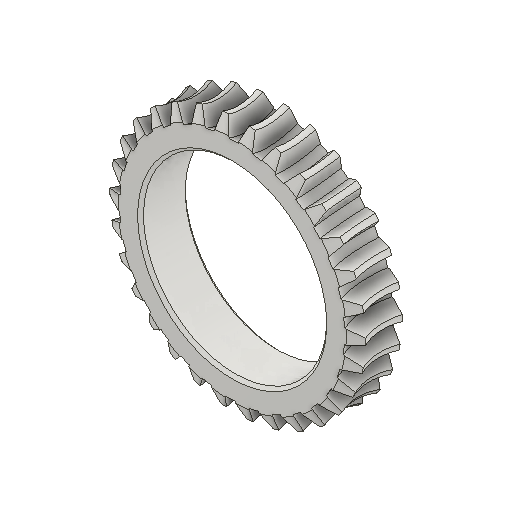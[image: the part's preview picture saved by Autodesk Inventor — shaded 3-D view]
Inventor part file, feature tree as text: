
AUTODESK INVENTOR PART (.ipt)
format: ipt  version: 2024.1 (Build 281209000, 209)  size: 570,368 bytes
history: native  units: mm (DEFAULTED — no unit token found)
features: other x10, plane x3, pattern_circular x1, extrude x1, chamfer x1, sketch x1, reference x1
ambient origin geometry x5: Origin, X Axis, Y Axis, Z Axis, Center Point
bodies: Solid1 (feature_tree)
feature tree (18):
  other  "Zahnebene"
  other  "Grundkörperskizze"
  other  "Grundkörper"
  other  "Grundkörper2"
  plane  "Work Plane13"
  other  "Zahn"
  pattern_circular  "Zahnanordnung"  [2 undecoded]
  plane  "Work Plane14"
  plane  "Work Plane15"
  extrude  "Extrusion1"  Depth=10.0mm
  chamfer  "Fasen1"  Distance=3.490659mm
  other  "Zahnskizze"
  other  "Srf1"
  sketch  "Skizze9"  dims[d35=90.0deg d37=-0.665682mm d38=28.975mm d39=3.490659mm d40=7.875mm d41=9.375mm d42=1.3mm d43=90.0deg d44=300.0mm d46=360.0deg d50=3.859836mm d68=28.975mm d69=0.0mm d73=0.0mm d75=1.047198mm d77=37.5mm d78=8.0mm d79=0.0mm d80=0.0mm d81=0.0mm d82=0.0mm d83=1.047198mm d84=0.0mm d85=180.0deg d86=28.975mm d87=42.95mm d89=16.25mm d90=90.0deg d92=8.0mm d93=28.975mm d94=0.3mm d95=10.0mm d96=0.0mm d97=0.5mm d98=2.0mm d99=45.0deg d100=30.7mm]
  reference  "Referenz1"
  other  "Flankendurchmesser"
  other  "Assembly_Planktoscope_Uc2version_wormdrive_V3.iam"
  other  "00_CCTV_Lens_Hikvision_50mm_2.8:1"
note: 2 required parameter values undecoded (feature->parameter linkage not recoverable at this tier; creation-order binding heuristic only, values carry confidence <= 0.55)
